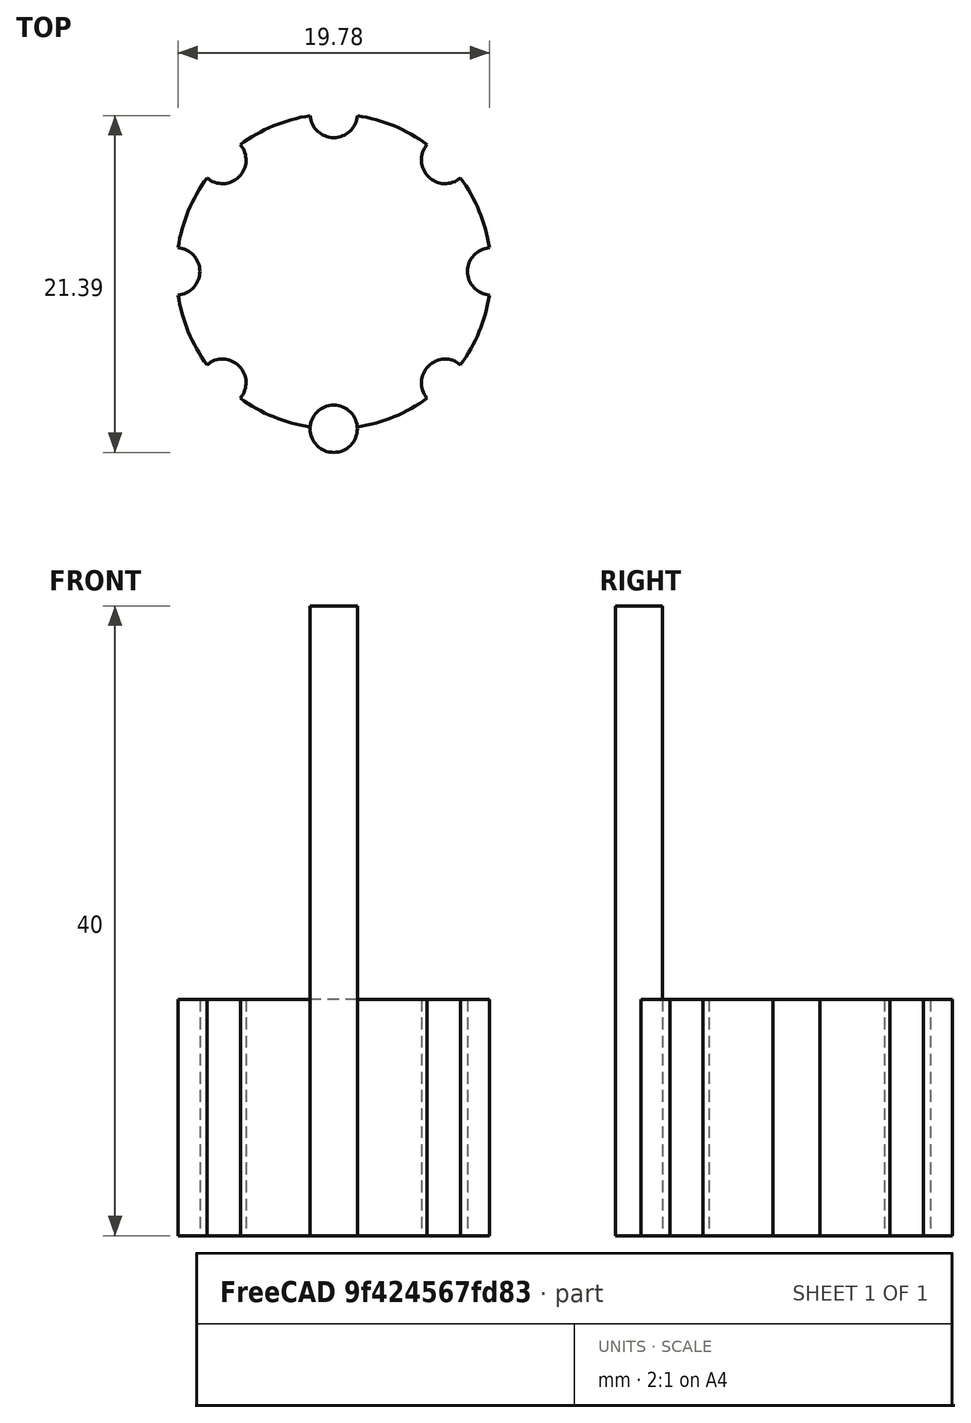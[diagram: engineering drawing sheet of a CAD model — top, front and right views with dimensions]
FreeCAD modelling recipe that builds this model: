
FCSTD DOCUMENT  (FreeCAD 1.0R39319 (Git))
Label: ojt1_t11r01_boto
License: All rights reserved
LicenseURL: https://en.wikipedia.org/wiki/All_rights_reserved
objects: Part::Cylinder×2, Part::FeaturePython×1, Part::Cut×1
note: 3 computed .brp shape members not serialized (recipe doc carries the construction recipe); baked Part::Feature solids carry a one-line shape summary decoded from their .brp

FEATURE [Part::Cylinder] Cylinder  label="Cilindre"
  Angle = 360
  AttacherType = Attacher::AttachEngine3D
  FirstAngle = 0
  Height = 15
  Placement = pos=(0,10,0) rot=(0,0,1;0rad)
  Radius = 10
  SecondAngle = 0
FEATURE [Part::Cylinder] Cylinder001  label="Cilindre001"
  Angle = 360
  AttacherType = Attacher::AttachEngine3D
  FirstAngle = 0
  Height = 40
  Radius = 1.5
  SecondAngle = 0
FEATURE [Part::FeaturePython] Array  # Draft array (typed FeaturePython)
  AlwaysSyncPlacement = false
  Angle = 360
  ArrayType = 1
  Axis = (0,0,1)
  Base = -> Cylinder001
  Center = (0,10,0)
  Count = 8
  ExpandArray = false
  Fuse = false
  IntervalAxis = (0,0,0)
  IntervalX = (50,0,0)
  IntervalY = (0,50,0)
  IntervalZ = (0,0,50)
  NumberCircles = 3
  NumberPolar = 8
  NumberX = 2
  NumberY = 2
  NumberZ = 1
  PlacementList = 8 placements: [(0,0,0),(7.07107,2.92893,0),(10,10,0),(7.07107,17.0711,0),(1.22465e-15,20,0),(-7.07107,17.0711,0),(-10,10,0),(-7.07107,2.92893,0)]
  RadialDistance = 50
  ScaleList = (8) [(1,1,1),(1,1,1),(1,1,1),(1,1,1),(1,1,1),(1,1,1),(1,1,1),(1,1,1)]
  Symmetry = 1
  TangentialDistance = 25
FEATURE [Part::Cut] Cut
  Base = -> Cylinder
  Refine = true
  Tool = -> Array
